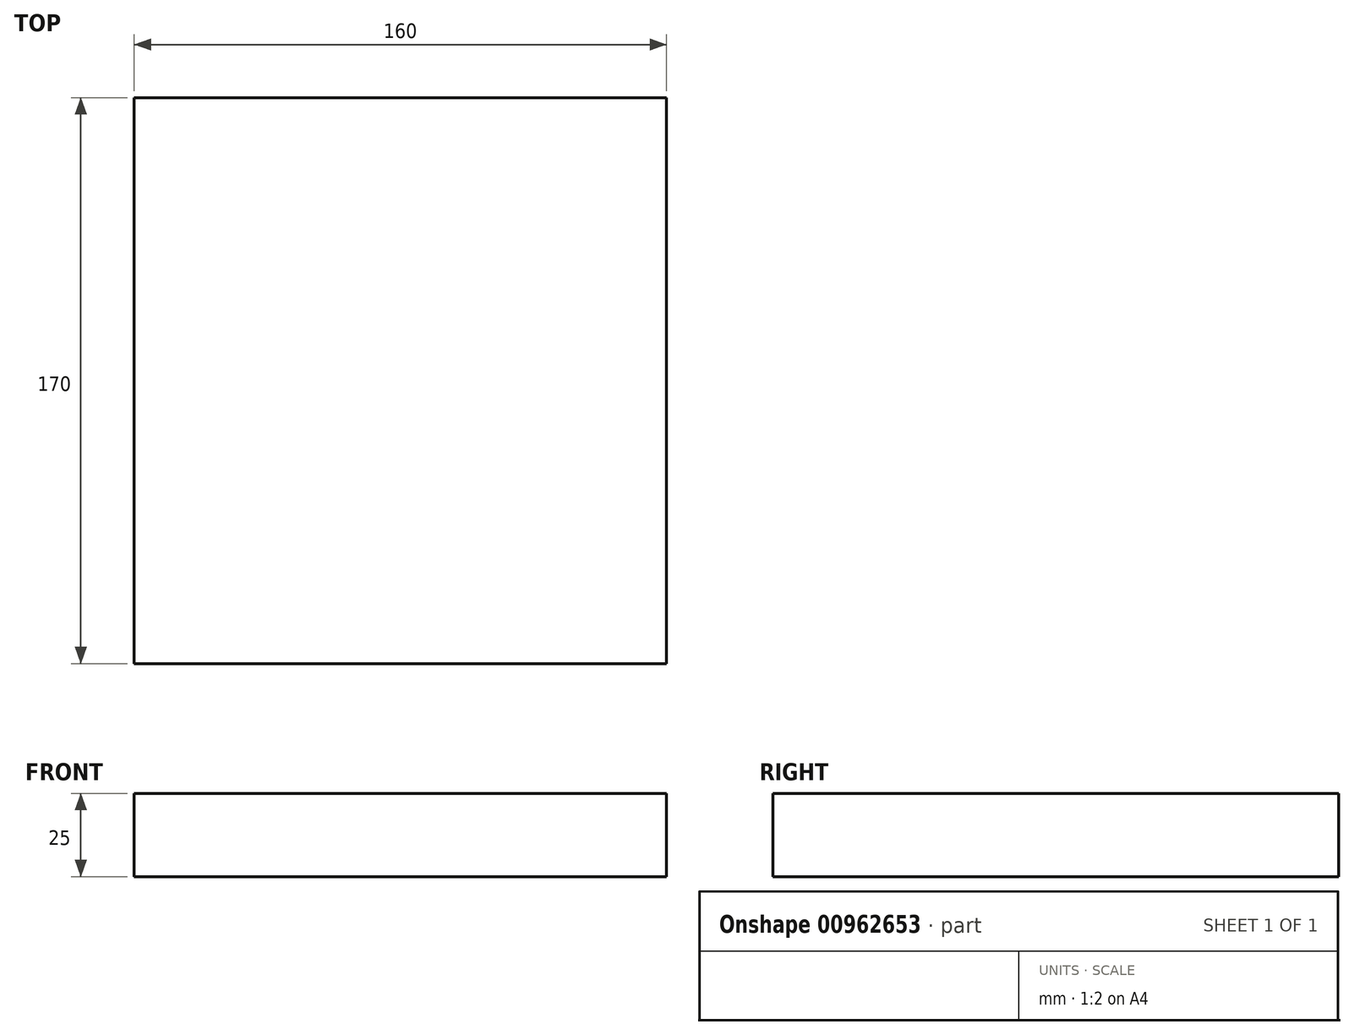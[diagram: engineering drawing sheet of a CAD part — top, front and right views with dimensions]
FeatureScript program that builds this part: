
annotation { "Feature Type Name" : "Feature", "Feature Type Description" : "" }
export const myFeature = defineFeature(function(context is Context, id is Id, definition is map)
    precondition{}
    {
        {
            var Q0;
            Q0=qCreatedBy(makeId("Top.planeOp"),FACE);
            var sketch = newSketch(context, id + "F0", { "sketchPlane" : qUnion([Q0])});
            skLineSegment(sketch, "E0.bottom", {"start": v(-69.55, 90.62) * mm, "end": v(90.45, 90.62) * mm});
            skLineSegment(sketch, "E0.top", {"start": v(-69.55, -79.38) * mm, "end": v(90.45, -79.38) * mm});
            skLineSegment(sketch, "E0.left", {"start": v(-69.55, 90.62) * mm, "end": v(-69.55, -79.38) * mm});
            skLineSegment(sketch, "E0.right", {"start": v(90.45, 90.62) * mm, "end": v(90.45, -79.38) * mm});
            skSolve(sketch);
        }
        {
            var Q0;
            Q0 = qSketchRegion(id + "F0", true);
            extrude(context, id + "F1", {"entities" : qUnion([Q0]), "depth" : 25 * mm, "offsetDistance" : 25 * mm});
        }
    });
